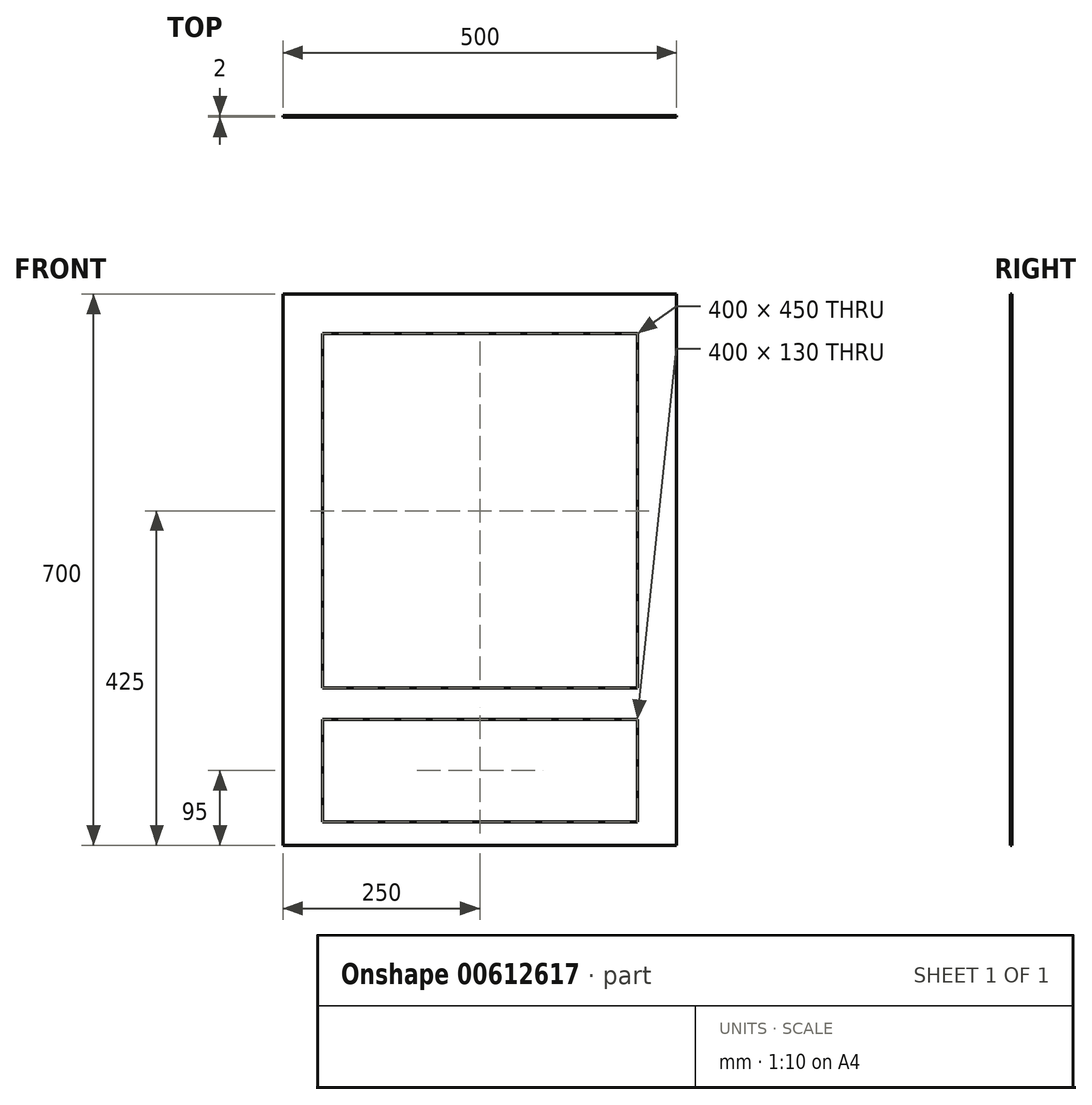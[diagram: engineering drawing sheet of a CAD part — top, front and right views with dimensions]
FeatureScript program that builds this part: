
annotation { "Feature Type Name" : "Feature", "Feature Type Description" : "" }
export const myFeature = defineFeature(function(context is Context, id is Id, definition is map)
    precondition{}
    {
        {
            var Q0;
            Q0=qCreatedBy(makeId("Front.planeOp"),FACE);
            var sketch = newSketch(context, id + "F0", { "sketchPlane" : qUnion([Q0])});
            skLineSegment(sketch, "E0.bottom", {"start": v(-250, 350) * mm, "end": v(250, 350) * mm});
            skLineSegment(sketch, "E0.top", {"start": v(-250, -350) * mm, "end": v(250, -350) * mm});
            skLineSegment(sketch, "E0.left", {"start": v(-250, 350) * mm, "end": v(-250, -350) * mm});
            skLineSegment(sketch, "E0.right", {"start": v(250, 350) * mm, "end": v(250, -350) * mm});
            skPoint(sketch, "E0.middle", {"position": v(0, 0) * mm});
            skLineSegment(sketch, "E1.bottom", {"start": v(-200, 300) * mm, "end": v(200, 300) * mm});
            skLineSegment(sketch, "E1.top", {"start": v(-200, -150) * mm, "end": v(200, -150) * mm});
            skLineSegment(sketch, "E1.left", {"start": v(-200, 300) * mm, "end": v(-200, -150) * mm});
            skLineSegment(sketch, "E1.right", {"start": v(200, 300) * mm, "end": v(200, -150) * mm});
            skSolve(sketch);
        }
        {
            var Q0;
            Q0=makeQuery(id+"F0.imprint","IMPRINT",FACE,{"disambiguationData":[TD([[makeQuery(id+"F0.imprint","IMPRINT",EDGE,{"derivedFrom":sQuery(id+"F0.wireOp",EDGE,"E0.bottom")}),-1.0]])]});
            extrude(context, id + "F1", {"entities" : qUnion([Q0]), "depth" : 2 * mm, "offsetDistance" : 25.4 * mm});
        }
        {
            var Q0;
            Q0=makeQuery(id+"F1.opExtrude","CAP_FACE",FACE,{"disambiguationData":[OSD([sQuery(id+"F0.wireOp",EDGE,"E0.bottom"),sQuery(id+"F0.wireOp",EDGE,"E0.top"),sQuery(id+"F0.wireOp",EDGE,"E0.left"),sQuery(id+"F0.wireOp",EDGE,"E0.right"),sQuery(id+"F0.wireOp",EDGE,"E1.bottom"),sQuery(id+"F0.wireOp",EDGE,"E1.top"),sQuery(id+"F0.wireOp",EDGE,"E1.left"),sQuery(id+"F0.wireOp",EDGE,"E1.right")])],"isStart":false});
            var sketch = newSketch(context, id + "F2", { "sketchPlane" : qUnion([Q0])});
            skLineSegment(sketch, "E2.bottom", {"start": v(-200, -190) * mm, "end": v(200, -190) * mm});
            skLineSegment(sketch, "E2.top", {"start": v(-200, -320) * mm, "end": v(200, -320) * mm});
            skLineSegment(sketch, "E2.left", {"start": v(-200, -190) * mm, "end": v(-200, -320) * mm});
            skLineSegment(sketch, "E2.right", {"start": v(200, -190) * mm, "end": v(200, -320) * mm});
            skSolve(sketch);
        }
        {
            var Q0;
            Q0=makeQuery(id+"F2.imprint","IMPRINT",FACE,{"disambiguationData":[TD([[makeQuery(id+"F2.imprint","IMPRINT",EDGE,{"derivedFrom":sQuery(id+"F2.wireOp",EDGE,"E2.bottom")}),-1.0]])]});
            extrude(context, id + "F3", {"entities" : qUnion([Q0]), "operationType" : NewBodyOperationType.REMOVE, "oppositeDirection" : true, "depth" : 4 * mm, "offsetDistance" : 25.4 * mm});
        }
    });
